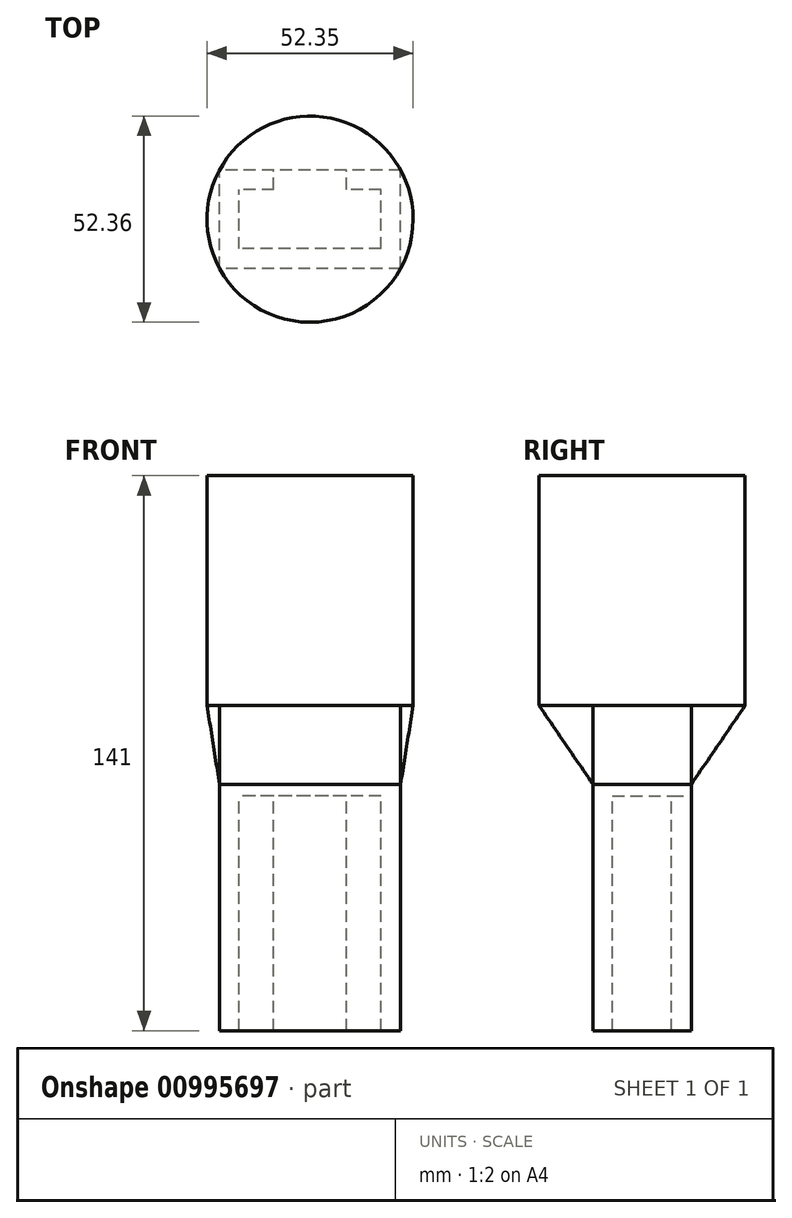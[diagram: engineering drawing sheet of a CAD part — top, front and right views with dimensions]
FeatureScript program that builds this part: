
annotation { "Feature Type Name" : "Feature", "Feature Type Description" : "" }
export const myFeature = defineFeature(function(context is Context, id is Id, definition is map)
    precondition{}
    {
        {
            var Q0;
            Q0=qCreatedBy(makeId("Top.planeOp"),FACE);
            var sketch = newSketch(context, id + "F0", { "sketchPlane" : qUnion([Q0])});
            skLineSegment(sketch, "E0.bottom", {"start": v(-10.21, 13.54) * mm, "end": v(-56.21, 13.54) * mm});
            skLineSegment(sketch, "E0.top", {"start": v(-10.21, 38.54) * mm, "end": v(-56.21, 38.54) * mm});
            skLineSegment(sketch, "E0.left", {"start": v(-10.21, 13.54) * mm, "end": v(-10.21, 38.54) * mm});
            skLineSegment(sketch, "E0.right", {"start": v(-56.21, 13.54) * mm, "end": v(-56.21, 38.54) * mm});
            skPoint(sketch, "E0.middle", {"position": v(-33.21, 26.04) * mm});
            skLineSegment(sketch, "E1.0", {"start": v(-15.21, 18.54) * mm, "end": v(-51.21, 18.54) * mm});
            skLineSegment(sketch, "E1.1", {"start": v(-15.21, 18.54) * mm, "end": v(-15.21, 33.54) * mm});
            skLineSegment(sketch, "E1.2", {"start": v(-15.21, 33.54) * mm, "end": v(-23.96, 33.54) * mm});
            skLineSegment(sketch, "E1.3", {"start": v(-51.21, 18.54) * mm, "end": v(-51.21, 33.54) * mm});
            skLineSegment(sketch, "E2", {"start": v(-42.46, 33.54) * mm, "end": v(-51.21, 33.54) * mm});
            skLineSegment(sketch, "E3", {"start": v(-23.96, 33.54) * mm, "end": v(-42.46, 33.54) * mm});
            skLineSegment(sketch, "E4", {"start": v(-42.46, 33.54) * mm, "end": v(-42.46, 38.54) * mm});
            skLineSegment(sketch, "E5", {"start": v(-23.96, 33.54) * mm, "end": v(-23.96, 38.54) * mm});
            skSolve(sketch);
        }
        {
            var Q0;
            Q0=makeQuery(id+"F0.imprint","IMPRINT",FACE,{"disambiguationData":[TD([[makeQuery(id+"F0.imprint","IMPRINT",EDGE,{"derivedFrom":sQuery(id+"F0.wireOp",EDGE,"E0.bottom")}),-1.0]])]});
            var Q1;
            Q1=makeQuery(id+"F0.imprint","IMPRINT",FACE,{"disambiguationData":[TD([[makeQuery(id+"F0.imprint","IMPRINT",EDGE,{"derivedFrom":sQuery(id+"F0.wireOp",EDGE,"E3")}),-1.0]])]});
            var Q2;
            Q2=makeQuery(id+"F0.imprint","IMPRINT",FACE,{"disambiguationData":[TD([[makeQuery(id+"F0.imprint","IMPRINT",EDGE,{"derivedFrom":sQuery(id+"F0.wireOp",EDGE,"E1.0")}),-1.0]])]});
            extrude(context, id + "F1", {"entities" : qUnion([Q0, Q1, Q2]), "depth" : 3 * mm, "offsetDistance" : 25 * mm});
        }
        {
            var Q0;
            Q0=makeQuery(id+"F1.opExtrude","CAP_FACE",FACE,{"disambiguationData":[OSD([sQuery(id+"F0.wireOp",EDGE,"E0.bottom"),sQuery(id+"F0.wireOp",EDGE,"E0.top"),sQuery(id+"F0.wireOp",EDGE,"E0.left"),sQuery(id+"F0.wireOp",EDGE,"E0.right")])],"isStart":false});
            cPlane(context, id + "F2", {"entities" : qUnion([Q0]), "cplaneType" : CPlaneType.OFFSET, "offset" : 20 * mm, "width" : 150 * mm, "height" : 150 * mm});
        }
        {
            var Q0;
            Q0=qCreatedBy(id+"F2.planeOp",FACE);
            var sketch = newSketch(context, id + "F3", { "sketchPlane" : qUnion([Q0])});
            skLineSegment(sketch, "E6.0.0", {"start": v(-10.21, 13.54) * mm, "end": v(-10.21, 38.54) * mm, "construction": true});
            skLineSegment(sketch, "E6.0.1", {"start": v(-10.21, 38.54) * mm, "end": v(-56.21, 38.54) * mm, "construction": true});
            skLineSegment(sketch, "E6.0.2", {"start": v(-56.21, 38.54) * mm, "end": v(-56.21, 38.54) * mm});
            skLineSegment(sketch, "E6.0.3", {"start": v(-56.21, 13.54) * mm, "end": v(-10.21, 13.54) * mm, "construction": true});
            skArc(sketch, "E7", {"start": v(-56.21, 38.54) * mm, "mid": v(-59.4, 26.04) * mm, "end": v(-56.21, 13.54) * mm});
            skArc(sketch, "E8", {"start": v(-10.21, 38.54) * mm, "mid": v(-33.21, 52.22) * mm, "end": v(-56.21, 38.54) * mm});
            skLineSegment(sketch, "E9", {"start": v(-10.21, 13.54) * mm, "end": v(-10.21, 13.54) * mm});
            skLineSegment(sketch, "E10", {"start": v(-56.21, 13.54) * mm, "end": v(-56.21, 13.54) * mm});
            skLineSegment(sketch, "E11", {"start": v(-56.21, 38.54) * mm, "end": v(-56.21, 13.54) * mm, "construction": true});
            skLineSegment(sketch, "E12", {"start": v(-10.21, 38.54) * mm, "end": v(-10.21, 38.54) * mm});
            skArc(sketch, "E13", {"start": v(-10.21, 13.54) * mm, "mid": v(-7.04, 26.04) * mm, "end": v(-10.21, 38.54) * mm});
            skArc(sketch, "E14", {"start": v(-56.21, 13.54) * mm, "mid": v(-33.21, -0.14) * mm, "end": v(-10.21, 13.54) * mm});
            skSolve(sketch);
        }
        {
            var Q0;
            Q0 = qSketchRegion(id + "F3", true);
            extrude(context, id + "F4", {"entities" : qUnion([Q0]), "depth" : 58.4 * mm, "offsetDistance" : 25 * mm});
        }
        {
            var Q1;
            Q1=makeQuery(id+"F1.opExtrude","CAP_FACE",FACE,{"disambiguationData":[OSD([sQuery(id+"F0.wireOp",EDGE,"E0.bottom"),sQuery(id+"F0.wireOp",EDGE,"E0.top"),sQuery(id+"F0.wireOp",EDGE,"E0.left"),sQuery(id+"F0.wireOp",EDGE,"E0.right")])],"isStart":false});
            var Q2;
            Q2=makeQuery(id+"F3.imprint","IMPRINT",FACE,{"disambiguationData":[TD([[makeQuery(id+"F3.imprint","IMPRINT",EDGE,{"derivedFrom":sQuery(id+"F3.wireOp",EDGE,"E7")}),1.0]])]});
            loft(context, id + "F5", {"operationType" : NewBodyOperationType.ADD, "sheetProfilesArray" : [{ "sheetProfileEntities" : qUnion([Q1]) }, { "sheetProfileEntities" : qUnion([Q2]) }]});
        }
        {
            var Q0;
            Q0=makeQuery(id+"F0.imprint","IMPRINT",FACE,{"disambiguationData":[TD([[makeQuery(id+"F0.imprint","IMPRINT",EDGE,{"derivedFrom":sQuery(id+"F0.wireOp",EDGE,"E0.bottom")}),-1.0]])]});
            extrude(context, id + "F6", {"entities" : qUnion([Q0]), "operationType" : NewBodyOperationType.ADD, "oppositeDirection" : true, "depth" : 59.6 * mm, "offsetDistance" : 25 * mm});
        }
    });
